# Revit family: KEUCO_34982010037
name_source: partatom
category: Allgemeines Modell
revit_build: Autodesk Revit 2016 (Build: 20150220_1215(x64)
units: mm (PartAtom-declared; Revit-internal decimal feet)

## family parameters
Arbeitsebenenbasiert = Ja
Beim Laden mit Abzugskörper schneiden = Nein
Bemaßung runder Anschluss = Durchmesser verwenden
Gemeinsam genutzt = Nein
Immer vertikal = Nein
Kann Basisbauteil für Bewehrung sein = Nein
Raumberechnungspunkt = Nein
Teiletyp = Normal

## types (6) — shared parameters
Beschreibung = zur Wandmontage
Sitzfläche nach oben klappbar,
Rückenlehne abnehmbar
Hersteller = KEUCO
Serie = Plan
URL = https://www.keuco.com
Verwendung = CA / DU
Vorgabe-Ansicht = 1219 mm
zero-valued in all types: Gewicht

## per-type parameters (varying)
| type | Ausschreibungstext | Material | Material Stahl |
| 34982010037 | KEUCO PLAN CARE Klappsitz 34982010037
schwarzgrauer (RAL 7021) Klappsitz 
aus Polypropylen zur Wandmontage,
in ästhetischem, funktionalem Design, 
für sicheres Sitzen im Duschbereich,
abnehmbare Rückenlehne zur leichten Reinigung,
Wandhalter und Sitzträger als Design-Element hochglanzverchromt,
antistatisch, leichte Reinigung,
nach oben klappbarer Sitz belastbar bis 110 kg,
Breite 363 mm, Länge der Sitzfläche 310 mm,
Ausladung 397 mm
Der Sitz wird verdeckt angebracht 

Das Befestigungsmaterial ist separat zu bestellen!

Zur Montage (je nach Ankergrund/Mauerwerk) 
unbedingt erforderlich:
2 x Befestigungs-Set 2 (Artikel-Nr. 34991000100)
oder
2 x Befestigungs-Set 5 (Artikel-Nr. 34991000200)
oder
2 x Befestigungs-Set 8 (Artikel-Nr. 34994000200)
oder 
1 x Befestigungs-Set 10 (Artikel-Nr., 34996000100) | Schwarzgrau | Stahl, verchromt |
| 34982010038 | KEUCO PLAN CARE Klappsitz 34982010038
lichtgrauer (RAL 7035) Klappsitz 
aus Polypropylen zur Wandmontage,
in ästhetischem, funktionalem Design, 
für sicheres Sitzen im Duschbereich,
abnehmbare Rückenlehne zur leichten Reinigung,
Wandhalter und Sitzträger als Design-Element hochglanzverchromt,
antistatisch, leichte Reinigung,
nach oben klappbarer Sitz belastbar bis 110 kg,
Breite 363 mm, Länge der Sitzfläche 310 mm,
Ausladung 397 mm
Der Sitz wird verdeckt angebracht 

Das Befestigungsmaterial ist separat zu bestellen!

Zur Montage (je nach Ankergrund/Mauerwerk) 
unbedingt erforderlich:
2 x Befestigungs-Set 2 (Artikel-Nr. 34991000100)
oder
2 x Befestigungs-Set 5 (Artikel-Nr. 34991000200)
oder
2 x Befestigungs-Set 8 (Artikel-Nr. 34994000200)
oder 
1 x Befestigungs-Set 10 (Artikel-Nr., 34996000100) | Lichtgrau (RAL 7035) | Stahl, verchromt |
| 34982010051 | KEUCO PLAN CARE Klappsitz 34982010051
weißer (RAL 9010) Klappsitz 
aus Polypropylen zur Wandmontage,
in ästhetischem, funktionalem Design, 
für sicheres Sitzen im Duschbereich,
abnehmbare Rückenlehne zur leichten Reinigung,
Wandhalter und Sitzträger als Design-Element hochglanzverchromt,
antistatisch, leichte Reinigung,
nach oben klappbarer Sitz belastbar bis 110 kg,
Breite 363 mm, Länge der Sitzfläche 310 mm,
Ausladung 397 mm
Der Sitz wird verdeckt angebracht 

Das Befestigungsmaterial ist separat zu bestellen!

Zur Montage (je nach Ankergrund/Mauerwerk) 
unbedingt erforderlich:
2 x Befestigungs-Set 2 (Artikel-Nr. 34991000100)
oder
2 x Befestigungs-Set 5 (Artikel-Nr. 34991000200)
oder
2 x Befestigungs-Set 8 (Artikel-Nr. 34994000200)
oder 
1 x Befestigungs-Set 10 (Artikel-Nr., 34996000100) | Weiß (RAL 9010) | Stahl, verchromt |
| 34982170037 | KEUCO PLAN CARE Klappsitz 34982170037
schwarzgrauer (RAL 7021) Klappsitz 
aus Polypropylen zur Wandmontage,
in ästhetischem, funktionalem Design, 
für sicheres Sitzen im Duschbereich,
abnehmbare Rückenlehne zur leichten Reinigung,
Wandhalter und Sitzträger als Design-Element 
aus silber-eloxiertem Aluminium (E6 EV1),
antistatisch, leichte Reinigung,
nach oben klappbarer Sitz belastbar bis 110 kg,
Breite 363 mm, Länge der Sitzfläche 310 mm,
Ausladung 397 mm
Der Sitz wird verdeckt angebracht 

Das Befestigungsmaterial ist separat zu bestellen!

Zur Montage (je nach Ankergrund/Mauerwerk) 
unbedingt erforderlich:
2 x Befestigungs-Set 2 (Artikel-Nr. 34991000100)
oder
2 x Befestigungs-Set 5 (Artikel-Nr. 34991000200)
oder
2 x Befestigungs-Set 8 (Artikel-Nr. 34994000200)
oder 
1 x Befestigungs-Set 10 (Artikel-Nr., 34996000100) | Schwarzgrau | Aluminium 1100-H18 |
| 34982170038 | KEUCO PLAN CARE Klappsitz 34982170038
lichtgrauer (RAL 7035) Klappsitz 
aus Polypropylen zur Wandmontage,
in ästhetischem, funktionalem Design, 
für sicheres Sitzen im Duschbereich,
abnehmbare Rückenlehne zur leichten Reinigung,
Wandhalter und Sitzträger als Design-Element 
aus silber-eloxiertem Aluminium (E6 EV1),
antistatisch, leichte Reinigung,
nach oben klappbarer Sitz belastbar bis 110 kg,
Breite 363 mm, Länge der Sitzfläche 310 mm,
Ausladung 397 mm
Der Sitz wird verdeckt angebracht 

Das Befestigungsmaterial ist separat zu bestellen!

Zur Montage (je nach Ankergrund/Mauerwerk) 
unbedingt erforderlich:
2 x Befestigungs-Set 2 (Artikel-Nr. 34991000100)
oder
2 x Befestigungs-Set 5 (Artikel-Nr. 34991000200)
oder
2 x Befestigungs-Set 8 (Artikel-Nr. 34994000200)
oder 
1 x Befestigungs-Set 10 (Artikel-Nr., 34996000100) | Weiß (RAL 9010) | Aluminium 1100-H18 |
| 34982170051 | KEUCO PLAN CARE Klappsitz 34982170051
weißter (RAL 9010) Klappsitz 
aus Polypropylen zur Wandmontage,
in ästhetischem, funktionalem Design, 
für sicheres Sitzen im Duschbereich,
abnehmbare Rückenlehne zur leichten Reinigung,
Wandhalter und Sitzträger als Design-Element 
aus silber-eloxiertem Aluminium (E6 EV1),
antistatisch, leichte Reinigung,
nach oben klappbarer Sitz belastbar bis 110 kg,
Breite 363 mm, Länge der Sitzfläche 310 mm,
Ausladung 397 mm
Der Sitz wird verdeckt angebracht 

Das Befestigungsmaterial ist separat zu bestellen!

Zur Montage (je nach Ankergrund/Mauerwerk) 
unbedingt erforderlich:
2 x Befestigungs-Set 2 (Artikel-Nr. 34991000100)
oder
2 x Befestigungs-Set 5 (Artikel-Nr. 34991000200)
oder
2 x Befestigungs-Set 8 (Artikel-Nr. 34994000200)
oder 
1 x Befestigungs-Set 10 (Artikel-Nr., 34996000100) | Weiß (RAL 9010) | Aluminium 1100-H18 |

note: column(s) folded — value = type name in every type: Artikelnummer

## geometry (parser evidence)
native form markers: Blend x4, Sweep x3
no freeform markers — native parametric forms only
